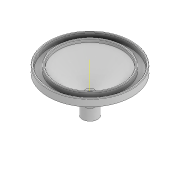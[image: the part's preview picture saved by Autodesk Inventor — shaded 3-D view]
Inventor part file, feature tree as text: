
AUTODESK INVENTOR PART (.ipt)
format: ipt  version: 2022 (Build 260153000, 153)  size: 178,176 bytes
history: native  units: mm
features: revolve x2, sketch x2, other x2, fillet x2
ambient origin geometry x8: Origin, YZ Plane, XZ Plane, XY Plane, X Axis, Y Axis, Z Axis, Center Point
bodies: Solid1 (feature_tree)
feature tree (8):
  revolve  "Revolution1"  [1 undecoded]
  sketch  "Sketch2"  dims[d3=90.0deg d6=35.0mm d7=1.0mm d8=5.0mm d9=5.0mm d10=5.0mm d11=2.0mm d12=7.0mm d13=2.0mm d14=90.0deg d15=2.0mm d16=0.5mm d17=4.4mm d18=7.58mm]
  other  "Work Axis1"
  other  "Work Axis2"
  revolve  "Revolution2"  [1 undecoded]
  fillet  "Fillet1"  Radius=1.0mm
  fillet  "Fillet2"  Radius=5.0mm
  sketch  "Sketch1"  dims[d1=3.18mm d2=20.0mm]
note: 2 required parameter values undecoded (feature->parameter linkage not recoverable at this tier; creation-order binding heuristic only, values carry confidence <= 0.55)
